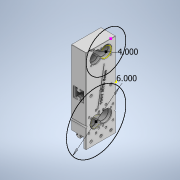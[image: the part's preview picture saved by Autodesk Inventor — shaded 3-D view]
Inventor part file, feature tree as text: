
AUTODESK INVENTOR PART (.ipt)
format: ipt  version: 2020 (Build 240168000, 168)  size: 862,208 bytes
history: native  units: in
note: dims shown in document units (in); Inventor stores cm internally (conversion verified against a paired STEP export)
features: reference x24, extrude x10, sketch x10, other x4, chamfer x1, fillet x1
ambient origin geometry x8: Origin, YZ Plane, XZ Plane, XY Plane, X Axis, Y Axis, Z Axis, Center Point
bodies: Solid1 (feature_tree)
feature tree (50):
  extrude  "Extrusion1"  Depth=5.0in
  extrude  "Extrusion2"  Depth=3.0in TaperAngle=0.0deg
  extrude  "Extrusion4"  TaperAngle=0.0deg  [1 undecoded]
  extrude  "Extrusion5"  Depth=1.126in
  extrude  "Extrusion6"  Depth=1.226in
  extrude  "Extrusion7"  Depth=1.126in
  extrude  "Extrusion8"  Depth=1.226in
  chamfer  "Chamfer3"  Distance=0.064in
  extrude  "Extrusion9"  Depth=0.165in
  fillet  "Fillet1"  [1 undecoded]
  sketch  "Sketch13"  dims[d50=1.4291in d51=0.165in d52=0.0in d53=0.0in]
  extrude  "Extrusion11"  Depth=1.0in
  extrude  "Extrusion12"  Depth=3.1496in TaperAngle=360.0deg
  reference  "Reference1"
  reference  "Reference2"
  reference  "Reference3"
  reference  "Reference4"
  reference  "Reference5"
  reference  "Reference6"
  reference  "Reference7"
  reference  "Reference8"
  reference  "Reference9"
  reference  "Reference10"
  reference  "Reference11"
  reference  "Reference12"
  reference  "Reference13"
  reference  "Reference14"
  reference  "Reference15"
  reference  "Reference16"
  reference  "Reference17"
  reference  "Reference18"
  reference  "Reference19"
  reference  "Reference20"
  reference  "Reference21"
  reference  "Reference22"
  reference  "Reference23"
  reference  "Reference24"
  sketch  "Sketch2"  dims[d0=1.5in d1=5.0in]
  sketch  "Sketch4"  dims[d2=0.2461in d3=3.0in d4=0.0in]
  sketch  "Sketch5"  dims[d7=0.2656in d24=0.0in d25=0.0in]
  sketch  "Sketch6"  dims[d31=1.023in d32=1.126in]
  sketch  "Sketch7"  dims[d33=0.314in d34=0.0in d35=1.226in]
  sketch  "Sketch8"  dims[d36=0.064in d37=0.0in d41=1.126in]
  sketch  "Sketch9"  dims[d42=0.314in d43=0.0in d44=1.226in d45=0.064in d46=0.0in]
  sketch  "Sketch14"  dims[d54=0.025in d55=0.125in d56=45.0deg d57=1.0in]
  sketch  "Sketch15"  dims[d58=0.196in d59=3.1496in d61=360.0deg d63=0.0in d64=0.0in d76=0.25in d77=3.5in d78=0.5in d79=0.5in d80=0.7874in d82=4.0in d83=1.1811in d85=1.0in d89=1.0in d90=2.0in d93=5.7096in d94=1.0in d95=1.0in d96=3.1496in d98=360.0deg d100=0.125in d101=4.0in d103=0.05in d104=1.0in d105=1.0in d106=0.05in d107=0.0in d108=0.1in d109=0.05in d110=0.0in d111=6.0in]
  other  "<userpath>\Documents\FRC\2020\ShooterPrototype.iam"
  other  "ShooterPrototype.iam"
  other  "9inSpacer:1"
  other  "1003-48-CL:4"
note: 2 required parameter values undecoded (feature->parameter linkage not recoverable at this tier; creation-order binding heuristic only, values carry confidence <= 0.55)
